# Revit family: Haworth_Epure_RoundTable_EU_PRELIMINARY
name_source: partatom
category: Furniture
units: mm (PartAtom-declared; Revit-internal decimal feet)

## family parameters
Always vertical = Yes
Cut with Voids When Loaded = No
OmniClass Number = 23.40.70.14.64.11
OmniClass Title = Office Furniture
Room Calculation Point = No
Shared = No
Work Plane-Based = No

## types (6) — shared parameters
Actual Height = 73 cm
Assembly Code = E2020200
Description = Haworth - Epure - Round Table
Leg Height = 70 cm
Manufacturer = Haworth
Revision Number = 1
Size = Verify Final Dim.w/ Haworth
Trim Finish = Haworth _ Metal _ Structured White EC
URL = https://www.haworth.com
URL - Product = https://www.haworth.com
Warranty = http://www.haworth.com

## per-type parameters (varying)
| type | Actual Diameter | Disc Base Support | Legs | Model | Radius |
| 110dia | 110 cm | No | Yes | EURT11 | 55 cm |
| 120dia | 120 cm | No | Yes | EURT12 | 60 cm |
| 80dia Round Base | 80 cm | Yes | No | EUG508 | 40 cm |
| 90dia Round Base | 90 cm | Yes | No | EUG509 | 45 cm |
| 100dia Round Base | 100 cm | Yes | No | EUG510 | 50 cm |
| 110dia  Round Base | 110 cm | Yes | No | EUG511 | 55 cm |

## geometry (parser evidence)
native form markers: Sweep x10
no freeform markers — native parametric forms only
